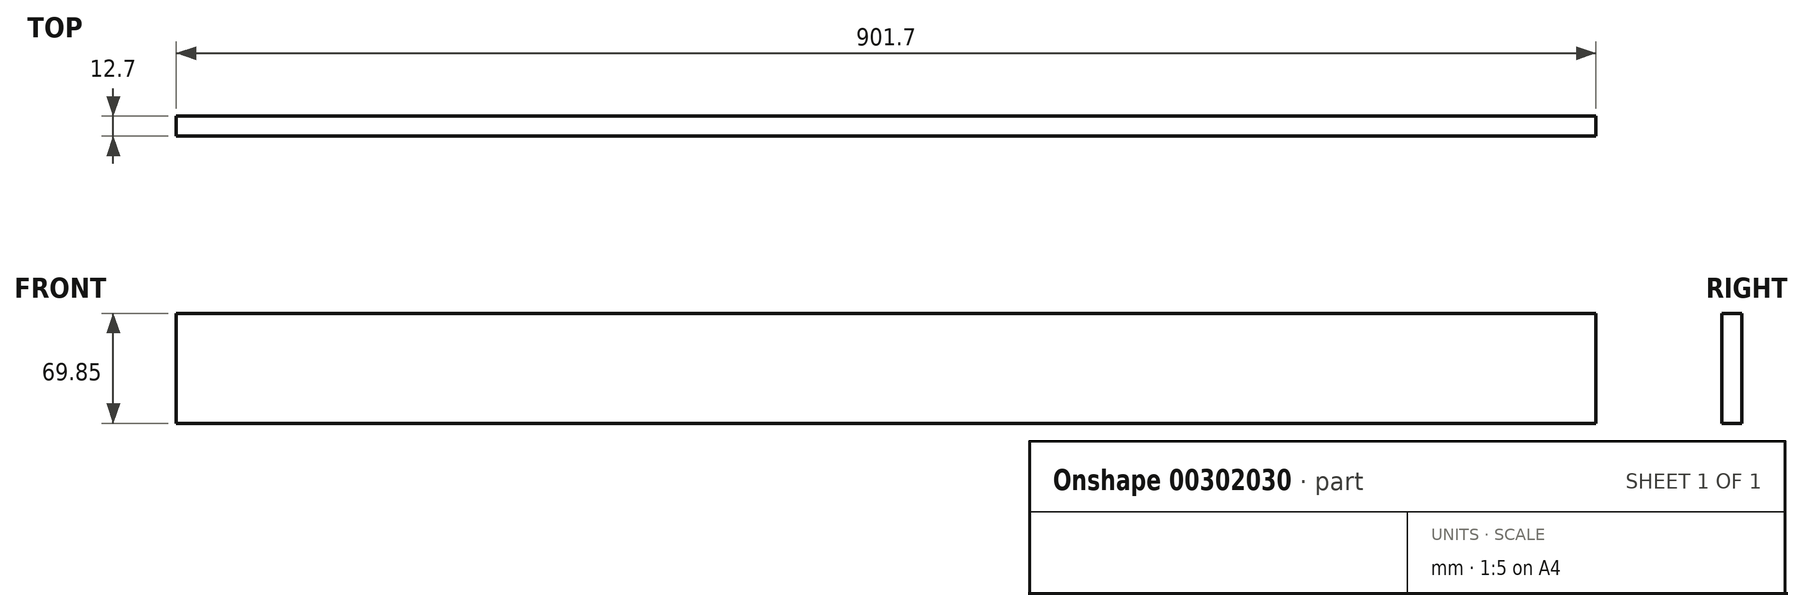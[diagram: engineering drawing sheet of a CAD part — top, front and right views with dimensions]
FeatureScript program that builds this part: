
annotation { "Feature Type Name" : "Feature", "Feature Type Description" : "" }
export const myFeature = defineFeature(function(context is Context, id is Id, definition is map)
    precondition{}
    {
        {
            var Q0;
            Q0=qCreatedBy(makeId("Top.planeOp"),FACE);
            var sketch = newSketch(context, id + "F0", { "sketchPlane" : qUnion([Q0])});
            skLineSegment(sketch, "E0.bottom", {"start": v(0, 0) * mm, "end": v(901.7, 0) * mm});
            skLineSegment(sketch, "E0.top", {"start": v(0, 12.7) * mm, "end": v(901.7, 12.7) * mm});
            skLineSegment(sketch, "E0.left", {"start": v(0, 0) * mm, "end": v(0, 12.7) * mm});
            skLineSegment(sketch, "E0.right", {"start": v(901.7, 0) * mm, "end": v(901.7, 12.7) * mm});
            skSolve(sketch);
        }
        {
            var Q0;
            Q0 = qSketchRegion(id + "F0", true);
            extrude(context, id + "F1", {"entities" : qUnion([Q0]), "depth" : 69.85 * mm});
        }
    });
